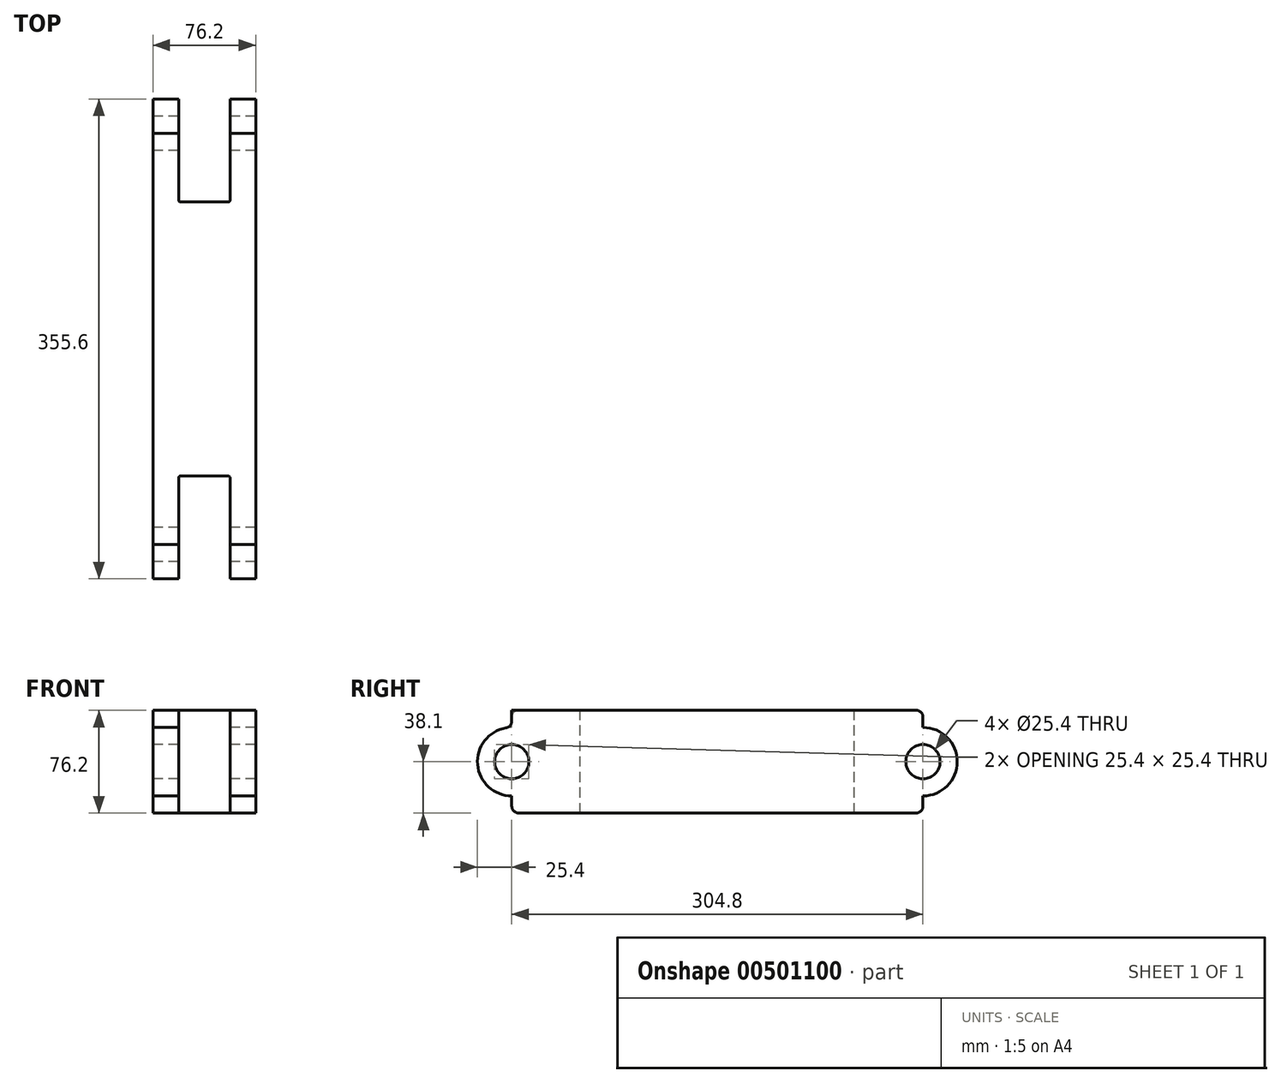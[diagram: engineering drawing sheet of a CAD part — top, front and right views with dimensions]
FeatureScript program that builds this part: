
annotation { "Feature Type Name" : "Feature", "Feature Type Description" : "" }
export const myFeature = defineFeature(function(context is Context, id is Id, definition is map)
    precondition{}
    {
        {
            var Q0;
            Q0=qCreatedBy(makeId("Right.planeOp"),FACE);
            var sketch = newSketch(context, id + "F0", { "sketchPlane" : qUnion([Q0])});
            skLineSegment(sketch, "E0.bottom", {"start": v(152.4, 38.1) * mm, "end": v(-152.4, 38.1) * mm});
            skLineSegment(sketch, "E0.top", {"start": v(152.4, -38.1) * mm, "end": v(-152.4, -38.1) * mm});
            skLineSegment(sketch, "E0.left", {"start": v(152.4, 38.1) * mm, "end": v(152.4, 25.4) * mm});
            skLineSegment(sketch, "E0.right", {"start": v(-152.4, 38.1) * mm, "end": v(-152.4, 25.4) * mm});
            skPoint(sketch, "E0.middle", {"position": v(0, 0) * mm});
            skArc(sketch, "E1", {"start": v(152.4, -25.4) * mm, "mid": v(177.8, 0) * mm, "end": v(152.4, 25.4) * mm});
            skCircle(sketch, "E2", {"center": v(152.4, 0) * mm, "radius": 12.7 * mm});
            skArc(sketch, "E3", {"start": v(-152.4, 25.4) * mm, "mid": v(-177.8, 0) * mm, "end": v(-152.4, -25.4) * mm});
            skCircle(sketch, "E4", {"center": v(-152.4, 0) * mm, "radius": 12.7 * mm});
            skLineSegment(sketch, "E5.trimOffspring", {"start": v(152.4, -25.4) * mm, "end": v(152.4, -38.1) * mm});
            skLineSegment(sketch, "E6.trimOffspring", {"start": v(-152.4, -25.4) * mm, "end": v(-152.4, -38.1) * mm});
            skSolve(sketch);
        }
        {
            var Q0;
            Q0=makeQuery(id+"F0.imprint","IMPRINT",FACE,{"disambiguationData":[TD([[makeQuery(id+"F0.imprint","IMPRINT",EDGE,{"derivedFrom":sQuery(id+"F0.wireOp",EDGE,"E0.bottom")}),1.0]])]});
            extrude(context, id + "F1", {"entities" : qUnion([Q0]), "endBound" : BoundingType.SYMMETRIC, "depth" : 76.2 * mm});
        }
        {
            var Q0;
            Q0=makeQuery(id+"F1.opExtrude","SWEPT_FACE",FACE,{"disambiguationData":[OSD([sQuery(id+"F0.wireOp",EDGE,"E0.bottom")])]});
            var sketch = newSketch(context, id + "F2", { "sketchPlane" : qUnion([Q0])});
            skLineSegment(sketch, "E7.bottom", {"start": v(19.05, 177.8) * mm, "end": v(-19.05, 177.8) * mm});
            skLineSegment(sketch, "E7.top", {"start": v(19.05, -177.8) * mm, "end": v(-19.05, -177.8) * mm});
            skLineSegment(sketch, "E7.left", {"start": v(19.05, 177.8) * mm, "end": v(19.05, -177.8) * mm});
            skLineSegment(sketch, "E7.right", {"start": v(-19.05, 177.8) * mm, "end": v(-19.05, -177.8) * mm});
            skPoint(sketch, "E7.middle", {"position": v(0, 0) * mm});
            skLineSegment(sketch, "E8", {"start": v(-19.05, 101.6) * mm, "end": v(19.05, 101.6) * mm});
            skLineSegment(sketch, "E9", {"start": v(-19.05, -101.6) * mm, "end": v(19.05, -101.6) * mm});
            skSolve(sketch);
        }
        {
            var Q0;
            {var subQ0=sQuery(id+"F2.wireOp",EDGE,"E7.bottom");Q0=makeQuery(id+"F2.imprint","IMPRINT",FACE,{"disambiguationData":[TD([[makeQuery(id+"F2.imprint","IMPRINT",EDGE,{"derivedFrom":subQ0}),1.0]])]});}
            var Q1;
            {var subQ0=sQuery(id+"F2.wireOp",EDGE,"E8");Q1=makeQuery(id+"F2.imprint","IMPRINT",FACE,{"disambiguationData":[TD([[makeQuery(id+"F2.imprint","IMPRINT",EDGE,{"derivedFrom":subQ0}),1.0]])]});}
            var Q2;
            {var subQ0=sQuery(id+"F2.wireOp",EDGE,"E9");Q2=makeQuery(id+"F2.imprint","IMPRINT",FACE,{"disambiguationData":[TD([[makeQuery(id+"F2.imprint","IMPRINT",EDGE,{"derivedFrom":subQ0}),-1.0]])]});}
            var Q3;
            {var subQ0=sQuery(id+"F2.wireOp",EDGE,"E7.top");Q3=makeQuery(id+"F2.imprint","IMPRINT",FACE,{"disambiguationData":[TD([[makeQuery(id+"F2.imprint","IMPRINT",EDGE,{"derivedFrom":subQ0}),-1.0]])]});}
            extrude(context, id + "F3", {"entities" : qUnion([Q0, Q1, Q2, Q3]), "operationType" : NewBodyOperationType.REMOVE, "oppositeDirection" : true, "depth" : 88.9 * mm});
        }
        {
            var Q0;
            {var subQ0=sQuery(id+"F0.wireOp",EDGE,"E5.trimOffspring");var subQ2=sQuery(id+"F0.wireOp",EDGE,"E0.top");var subQ4=sQuery(id+"F2.wireOp",EDGE,"E7.left");Q0=makeQuery(id+"F3.boolean.opBoolean","SPLIT",EDGE,{"disambiguationData":[TD([makeQuery(id+"F3.opExtrude","SWEPT_FACE",FACE,{"disambiguationData":[OSD([subQ4]),TDD([makeQuery(id+"F2.imprint","IMPRINT",EDGE,{"disambiguationData":[TD([[makeQuery(id+"F2.imprint","INTERSECT",VERTEX,{"derivedFrom":[sQuery(id+"F2.wireOp",EDGE,"E7.bottom"),subQ4]}),-1.0]])],"derivedFrom":subQ4}),makeQuery(id+"F2.imprint","IMPRINT",EDGE,{"disambiguationData":[TD([[makeQuery(id+"F2.imprint","INTERSECT",VERTEX,{"derivedFrom":[subQ4,sQuery(id+"F2.wireOp",EDGE,"E8")]}),1.0]])],"derivedFrom":subQ4})])]})])],"derivedFrom":makeQuery(id+"F1.opExtrude","SWEPT_EDGE",EDGE,{"disambiguationData":[OSD([subQ2,subQ0])]})});}
            var Q1;
            {var subQ0=sQuery(id+"F0.wireOp",EDGE,"E5.trimOffspring");var subQ2=sQuery(id+"F0.wireOp",EDGE,"E0.top");var subQ4=sQuery(id+"F2.wireOp",EDGE,"E7.right");Q1=makeQuery(id+"F3.boolean.opBoolean","SPLIT",EDGE,{"disambiguationData":[TD([makeQuery(id+"F3.opExtrude","SWEPT_FACE",FACE,{"disambiguationData":[OSD([subQ4]),TDD([makeQuery(id+"F2.imprint","IMPRINT",EDGE,{"disambiguationData":[TD([[makeQuery(id+"F2.imprint","INTERSECT",VERTEX,{"derivedFrom":[sQuery(id+"F2.wireOp",EDGE,"E7.bottom"),subQ4]}),-1.0]])],"derivedFrom":subQ4}),makeQuery(id+"F2.imprint","IMPRINT",EDGE,{"disambiguationData":[TD([[makeQuery(id+"F2.imprint","INTERSECT",VERTEX,{"derivedFrom":[subQ4,sQuery(id+"F2.wireOp",EDGE,"E8")]}),1.0]])],"derivedFrom":subQ4})])]})])],"derivedFrom":makeQuery(id+"F1.opExtrude","SWEPT_EDGE",EDGE,{"disambiguationData":[OSD([subQ2,subQ0])]})});}
            var Q2;
            {var subQ0=sQuery(id+"F0.wireOp",EDGE,"E0.bottom");var subQ1=sQuery(id+"F0.wireOp",EDGE,"E0.left");var subQ2=sQuery(id+"F2.wireOp",EDGE,"E7.right");var subQ3=makeQuery(id+"F1.opExtrude","SWEPT_EDGE",EDGE,{"disambiguationData":[OSD([subQ0,subQ1])]});Q2=makeQuery(id+"F3.boolean.opBoolean","SPLIT",EDGE,{"disambiguationData":[TD([makeQuery(id+"F3.opExtrude","SWEPT_FACE",FACE,{"disambiguationData":[OSD([subQ2]),TDD([makeQuery(id+"F2.imprint","IMPRINT",EDGE,{"disambiguationData":[TD([[makeQuery(id+"F2.imprint","INTERSECT",VERTEX,{"derivedFrom":[sQuery(id+"F2.wireOp",EDGE,"E7.bottom"),subQ2]}),-1.0]])],"derivedFrom":subQ2}),makeQuery(id+"F2.imprint","IMPRINT",EDGE,{"disambiguationData":[TD([[makeQuery(id+"F2.imprint","INTERSECT",VERTEX,{"derivedFrom":[subQ2,sQuery(id+"F2.wireOp",EDGE,"E8")]}),1.0]])],"derivedFrom":subQ2})])]})])],"derivedFrom":subQ3});}
            var Q3;
            {var subQ0=sQuery(id+"F0.wireOp",EDGE,"E0.bottom");var subQ1=sQuery(id+"F0.wireOp",EDGE,"E0.left");var subQ2=sQuery(id+"F2.wireOp",EDGE,"E7.left");var subQ3=makeQuery(id+"F1.opExtrude","SWEPT_EDGE",EDGE,{"disambiguationData":[OSD([subQ0,subQ1])]});Q3=makeQuery(id+"F3.boolean.opBoolean","SPLIT",EDGE,{"disambiguationData":[TD([makeQuery(id+"F3.opExtrude","SWEPT_FACE",FACE,{"disambiguationData":[OSD([subQ2]),TDD([makeQuery(id+"F2.imprint","IMPRINT",EDGE,{"disambiguationData":[TD([[makeQuery(id+"F2.imprint","INTERSECT",VERTEX,{"derivedFrom":[sQuery(id+"F2.wireOp",EDGE,"E7.bottom"),subQ2]}),-1.0]])],"derivedFrom":subQ2}),makeQuery(id+"F2.imprint","IMPRINT",EDGE,{"disambiguationData":[TD([[makeQuery(id+"F2.imprint","INTERSECT",VERTEX,{"derivedFrom":[subQ2,sQuery(id+"F2.wireOp",EDGE,"E8")]}),1.0]])],"derivedFrom":subQ2})])]})])],"derivedFrom":subQ3});}
            var Q4;
            {var subQ0=sQuery(id+"F0.wireOp",EDGE,"E6.trimOffspring");var subQ2=sQuery(id+"F0.wireOp",EDGE,"E0.top");var subQ4=sQuery(id+"F2.wireOp",EDGE,"E7.left");Q4=makeQuery(id+"F3.boolean.opBoolean","SPLIT",EDGE,{"disambiguationData":[TD([makeQuery(id+"F3.opExtrude","SWEPT_FACE",FACE,{"disambiguationData":[OSD([subQ4]),TDD([makeQuery(id+"F2.imprint","IMPRINT",EDGE,{"disambiguationData":[TD([[makeQuery(id+"F2.imprint","INTERSECT",VERTEX,{"derivedFrom":[subQ4,sQuery(id+"F2.wireOp",EDGE,"E9")]}),-1.0]])],"derivedFrom":subQ4}),makeQuery(id+"F2.imprint","IMPRINT",EDGE,{"disambiguationData":[TD([[makeQuery(id+"F2.imprint","INTERSECT",VERTEX,{"derivedFrom":[sQuery(id+"F2.wireOp",EDGE,"E7.top"),subQ4]}),1.0]])],"derivedFrom":subQ4})])]})])],"derivedFrom":makeQuery(id+"F1.opExtrude","SWEPT_EDGE",EDGE,{"disambiguationData":[OSD([subQ2,subQ0])]})});}
            var Q5;
            {var subQ0=sQuery(id+"F0.wireOp",EDGE,"E6.trimOffspring");var subQ2=sQuery(id+"F0.wireOp",EDGE,"E0.top");var subQ4=sQuery(id+"F2.wireOp",EDGE,"E7.right");Q5=makeQuery(id+"F3.boolean.opBoolean","SPLIT",EDGE,{"disambiguationData":[TD([makeQuery(id+"F3.opExtrude","SWEPT_FACE",FACE,{"disambiguationData":[OSD([subQ4]),TDD([makeQuery(id+"F2.imprint","IMPRINT",EDGE,{"disambiguationData":[TD([[makeQuery(id+"F2.imprint","INTERSECT",VERTEX,{"derivedFrom":[subQ4,sQuery(id+"F2.wireOp",EDGE,"E9")]}),-1.0]])],"derivedFrom":subQ4}),makeQuery(id+"F2.imprint","IMPRINT",EDGE,{"disambiguationData":[TD([[makeQuery(id+"F2.imprint","INTERSECT",VERTEX,{"derivedFrom":[sQuery(id+"F2.wireOp",EDGE,"E7.top"),subQ4]}),1.0]])],"derivedFrom":subQ4})])]})])],"derivedFrom":makeQuery(id+"F1.opExtrude","SWEPT_EDGE",EDGE,{"disambiguationData":[OSD([subQ2,subQ0])]})});}
            var Q6;
            {var subQ0=sQuery(id+"F0.wireOp",EDGE,"E3");var subQ1=sQuery(id+"F0.wireOp",EDGE,"E0.right");var subQ3=sQuery(id+"F2.wireOp",EDGE,"E7.left");Q6=makeQuery(id+"F3.boolean.opBoolean","SPLIT",EDGE,{"disambiguationData":[TD([makeQuery(id+"F3.opExtrude","SWEPT_FACE",FACE,{"disambiguationData":[OSD([subQ3]),TDD([makeQuery(id+"F2.imprint","IMPRINT",EDGE,{"disambiguationData":[TD([[makeQuery(id+"F2.imprint","INTERSECT",VERTEX,{"derivedFrom":[subQ3,sQuery(id+"F2.wireOp",EDGE,"E9")]}),-1.0]])],"derivedFrom":subQ3}),makeQuery(id+"F2.imprint","IMPRINT",EDGE,{"disambiguationData":[TD([[makeQuery(id+"F2.imprint","INTERSECT",VERTEX,{"derivedFrom":[sQuery(id+"F2.wireOp",EDGE,"E7.top"),subQ3]}),1.0]])],"derivedFrom":subQ3})])]})])],"derivedFrom":makeQuery(id+"F1.opExtrude","SWEPT_EDGE",EDGE,{"disambiguationData":[OSD([subQ1,subQ0])]})});}
            var Q7;
            {var subQ0=sQuery(id+"F0.wireOp",EDGE,"E0.bottom");var subQ1=sQuery(id+"F0.wireOp",EDGE,"E0.right");var subQ2=sQuery(id+"F2.wireOp",EDGE,"E7.right");var subQ3=makeQuery(id+"F1.opExtrude","SWEPT_EDGE",EDGE,{"disambiguationData":[OSD([subQ0,subQ1])]});Q7=makeQuery(id+"F3.boolean.opBoolean","SPLIT",EDGE,{"disambiguationData":[TD([makeQuery(id+"F3.opExtrude","SWEPT_FACE",FACE,{"disambiguationData":[OSD([subQ2]),TDD([makeQuery(id+"F2.imprint","IMPRINT",EDGE,{"disambiguationData":[TD([[makeQuery(id+"F2.imprint","INTERSECT",VERTEX,{"derivedFrom":[subQ2,sQuery(id+"F2.wireOp",EDGE,"E9")]}),-1.0]])],"derivedFrom":subQ2}),makeQuery(id+"F2.imprint","IMPRINT",EDGE,{"disambiguationData":[TD([[makeQuery(id+"F2.imprint","INTERSECT",VERTEX,{"derivedFrom":[sQuery(id+"F2.wireOp",EDGE,"E7.top"),subQ2]}),1.0]])],"derivedFrom":subQ2})])]})])],"derivedFrom":subQ3});}
            fillet(context, id + "F4", {"entities" : qUnion([Q0, Q1, Q2, Q3, Q4, Q5, Q6, Q7]), "radius" : 5.08 * mm, "tangentPropagation" : true, "allowEdgeOverflow" : false});
        }
        {
            var Q0;
            Q0=makeQuery(id+"F3.boolean.opBoolean","COPY",EDGE,{"derivedFrom":makeQuery(id+"F3.opExtrude","SWEPT_EDGE",EDGE,{"disambiguationData":[OSD([sQuery(id+"F2.wireOp",EDGE,"E7.left"),sQuery(id+"F2.wireOp",EDGE,"E8")])]})});
            var Q1;
            Q1=makeQuery(id+"F3.boolean.opBoolean","COPY",EDGE,{"derivedFrom":makeQuery(id+"F3.opExtrude","SWEPT_EDGE",EDGE,{"disambiguationData":[OSD([sQuery(id+"F2.wireOp",EDGE,"E7.right"),sQuery(id+"F2.wireOp",EDGE,"E8")])]})});
            var Q2;
            Q2=makeQuery(id+"F3.boolean.opBoolean","COPY",EDGE,{"derivedFrom":makeQuery(id+"F3.opExtrude","SWEPT_EDGE",EDGE,{"disambiguationData":[OSD([sQuery(id+"F2.wireOp",EDGE,"E7.left"),sQuery(id+"F2.wireOp",EDGE,"E9")])]})});
            var Q3;
            Q3=makeQuery(id+"F3.boolean.opBoolean","COPY",EDGE,{"derivedFrom":makeQuery(id+"F3.opExtrude","SWEPT_EDGE",EDGE,{"disambiguationData":[OSD([sQuery(id+"F2.wireOp",EDGE,"E7.right"),sQuery(id+"F2.wireOp",EDGE,"E9")])]})});
            fillet(context, id + "F5", {"entities" : qUnion([Q0, Q1, Q2, Q3]), "radius" : 1.27 * mm, "tangentPropagation" : true, "allowEdgeOverflow" : false});
        }
    });
